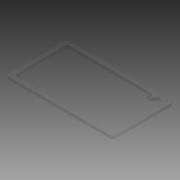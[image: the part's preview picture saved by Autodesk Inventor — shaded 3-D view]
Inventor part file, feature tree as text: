
AUTODESK INVENTOR PART (.ipt)
format: ipt  version: 2015 (Build 190159000, 159)  size: 198,656 bytes
history: native  units: mm
features: extrude x2, fillet x2, reference x1
ambient origin geometry x8: Origin, YZ Plane, XZ Plane, XY Plane, X Axis, Y Axis, Z Axis, Center Point
bodies: Solid1 (feature_tree)
feature tree (5):
  extrude  "Extrusión1"  Depth=2.0mm
  fillet  "Empalme1"  Radius=3.25mm
  extrude  "Extrusión2"  Depth=5.0mm
  fillet  "Empalme3"  Radius=2.0mm
  reference  "Referencia1"
